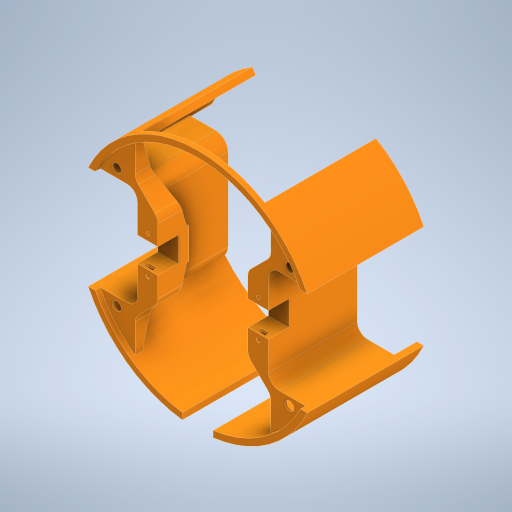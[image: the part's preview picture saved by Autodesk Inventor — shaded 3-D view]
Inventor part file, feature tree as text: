
AUTODESK INVENTOR PART (.ipt)
format: ipt  version: 2023.1 (Build 271208000, 208)  size: 740,864 bytes
history: native  units: mm
features: extrude x13, sketch x10, chamfer x6, projected_geometry x4, other x1, fillet x1, mirror x1
ambient origin geometry x8: Origin, YZ Plane, XZ Plane, XY Plane, X Axis, Y Axis, Z Axis, Center Point
bodies: Body1 (feature_tree)
feature tree (36):
  other  "Sólido1"
  extrude  "Extrusión1"  Depth=3.0mm
  extrude  "Extrusión2"  Depth=50.0mm
  extrude  "Extrusión3"  Depth=9.0mm
  fillet  "Empalme12"  Radius=15.0mm
  extrude  "Extrusión20"  Depth=2.5mm
  extrude  "Extrusión21"  Depth=7.0mm TaperAngle=0.0deg
  sketch  "Boceto16"  dims[d3=50.0mm d4=18.0mm]
  extrude  "Extrusión22"  Depth=5.0mm
  chamfer  "Chaflán3"  Distance=83.82mm
  chamfer  "Chaflán4"  Distance=26.04mm
  mirror  "Simetría6"
  chamfer  "Chaflán5"  Distance=1.079663mm
  chamfer  "Chaflán6"  [1 undecoded]
  chamfer  "Chaflán7"  Distance=10.0mm
  chamfer  "Chaflán8"  Distance=2.0mm
  extrude  "Extrusión24"  Depth=10.0mm
  extrude  "Extrusión25"  Depth=12.15mm
  sketch  "Boceto19"  dims[d13=1.0mm d14=0.0mm d15=7.0mm d16=0.0mm]
  extrude  "Extrusión26"  Depth=10.0mm
  extrude  "Extrusión28"  Depth=1.5mm
  extrude  "Extrusión29"  Depth=1.5mm
  sketch  "Boceto23"  dims[d116=110.0mm]
  sketch  "Boceto24"  dims[d117=41.91mm]
  extrude  "Extrusión30"  Depth=5.0mm
  extrude  "Extrusión31"  Depth=10.0mm TaperAngle=0.0deg
  sketch  "Boceto25"  dims[d119=57.92mm d120=83.82mm d121=26.04mm d131=1.079663mm d132=0.0mm d133=10.0mm d134=2.0mm d135=18.0mm d136=12.15mm d137=18.0mm d138=1.5mm d139=1.5mm d140=5.0mm d141=10.0mm d142=0.0mm d151=5.0mm d152=0.0mm d154=4.25mm d155=4.25mm d156=1.0mm d157=3.0mm d158=0.0mm d159=10.0mm d160=15.0mm d161=45.0deg d162=10.0mm d163=35.0mm d164=45.0deg d165=10.0mm d166=35.0mm d167=45.0deg d168=7.0mm d169=15.0mm d170=45.0deg d173=10.0mm d174=35.0mm d175=45.0deg d176=10.0mm d177=35.0mm d178=45.0deg d180=4.0mm d181=2.0mm d182=1.0mm d183=0.0mm d184=4.0mm d185=2.0mm d186=10.0mm d187=0.0mm d188=4.25mm d189=4.0mm d190=2.0mm d191=20.0mm d192=5.0mm d193=0.0mm d194=0.0mm d197=47.0mm d198=0.0mm d199=42.0mm d200=0.0mm d201=1.0mm d202=1.0mm d203=35.0mm d204=0.0mm d205=1.0mm d206=1.0mm d207=10.0mm d208=0.0mm d42=0.5mm d43=0.872665mm d44=0.5mm d45=0.872665mm d125=0.5mm d126=0.872665mm d127=0.5mm d128=0.872665mm]
  sketch  "Boceto15"  dims[d0=111.5mm d1=3.0mm]
  projected_geometry  "Contorno proyectado16"
  projected_geometry  "Contorno proyectado17"
  projected_geometry  "Contorno proyectado18"
  projected_geometry  "Contorno proyectado19"
  sketch  "Boceto17"  dims[d5=4.5mm d8=9.0mm d9=15.0mm]
  sketch  "Boceto18"  dims[d10=2.5mm d11=0.0mm d12=60.0mm]
  sketch  "Boceto20"  dims[d24=20.0mm d28=5.0mm]
  sketch  "Boceto22"  dims[d76=0.5mm]
note: 1 required parameter value undecoded (feature->parameter linkage not recoverable at this tier; creation-order binding heuristic only, values carry confidence <= 0.55)
